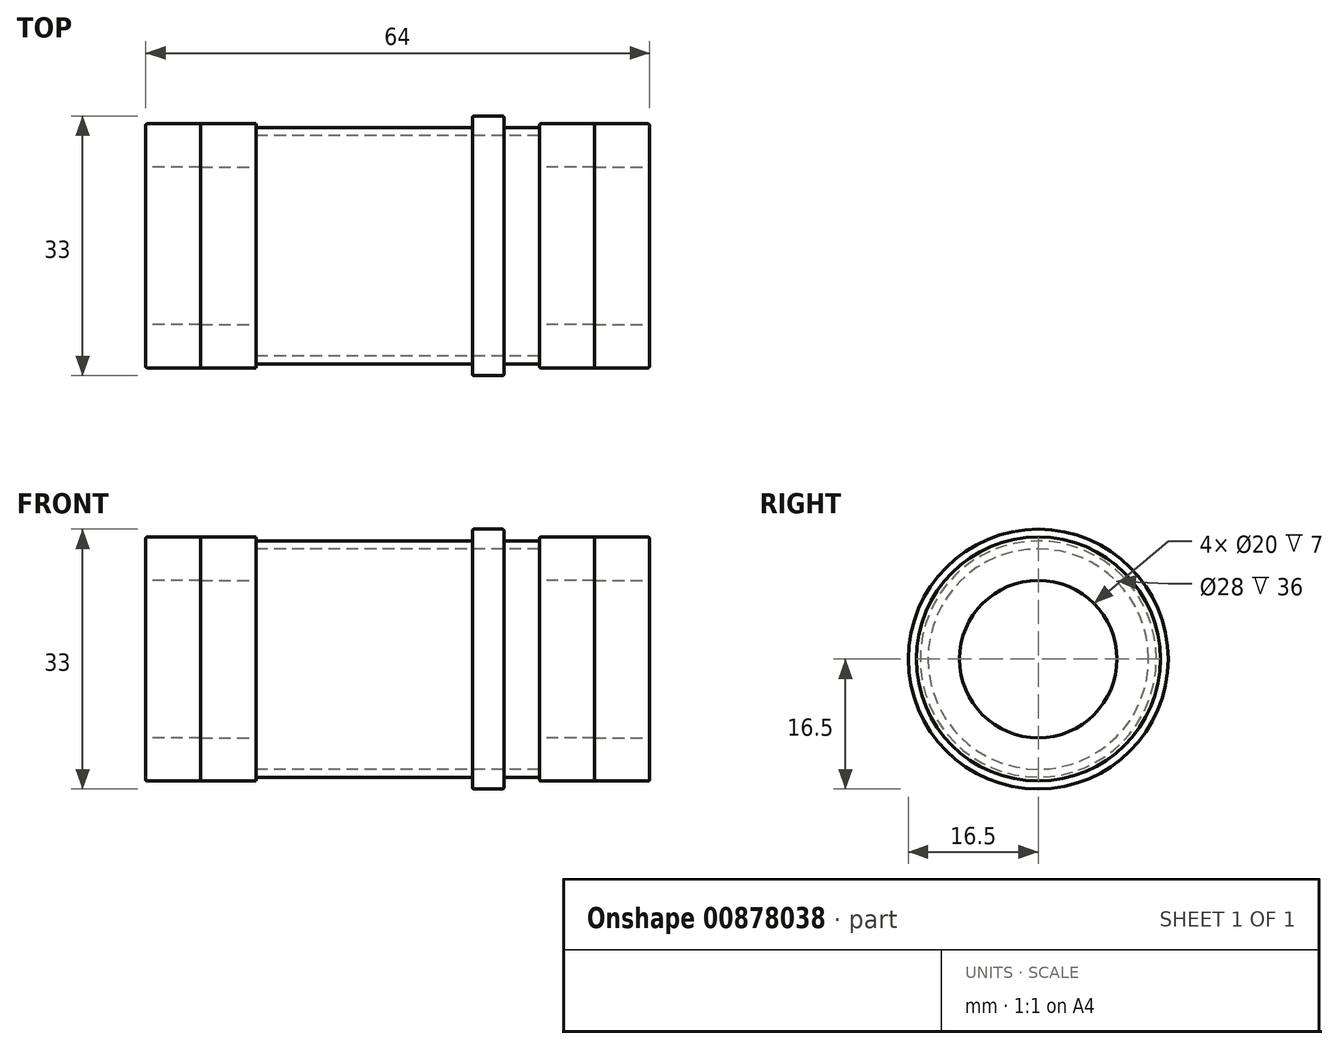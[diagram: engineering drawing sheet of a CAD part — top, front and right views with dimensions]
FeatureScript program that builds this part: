
annotation { "Feature Type Name" : "Feature", "Feature Type Description" : "" }
export const myFeature = defineFeature(function(context is Context, id is Id, definition is map)
    precondition{}
    {
        {
            var Q0;
            Q0=qCreatedBy(makeId("Right.planeOp"),FACE);
            var sketch = newSketch(context, id + "F0", { "sketchPlane" : qUnion([Q0])});
            skCircle(sketch, "E0", {"center": v(0, 0) * mm, "radius": 15 * mm});
            skCircle(sketch, "E1", {"center": v(0, 0) * mm, "radius": 14 * mm});
            skSolve(sketch);
        }
        {
            var Q0;
            Q0=makeQuery(id+"F0.imprint","IMPRINT",FACE,{"disambiguationData":[TD([[makeQuery(id+"F0.imprint","IMPRINT",EDGE,{"derivedFrom":sQuery(id+"F0.wireOp",EDGE,"E0")}),1.0]])]});
            extrude(context, id + "F1", {"entities" : qUnion([Q0]), "depth" : 36 * mm, "offsetDistance" : 25 * mm});
        }
        {
            var Q0;
            Q0=qCreatedBy(makeId("Right.planeOp"),FACE);
            var sketch = newSketch(context, id + "F2", { "sketchPlane" : qUnion([Q0])});
            skCircle(sketch, "E2", {"center": v(0, 0) * mm, "radius": 10 * mm});
            skCircle(sketch, "E3", {"center": v(0, 0) * mm, "radius": 15.5 * mm});
            skSolve(sketch);
        }
        {
            var Q0;
            Q0=makeQuery(id+"F2.imprint","IMPRINT",FACE,{"disambiguationData":[TD([[makeQuery(id+"F2.imprint","IMPRINT",EDGE,{"derivedFrom":sQuery(id+"F2.wireOp",EDGE,"E2")}),-1.0]])]});
            extrude(context, id + "F3", {"entities" : qUnion([Q0]), "oppositeDirection" : true, "depth" : 7 * mm, "offsetDistance" : 25 * mm});
        }
        {
            var Q0;
            Q0=makeQuery(id+"F3.opExtrude","SWEPT_BODY",BODY,{"disambiguationData":[OSD([sQuery(id+"F2.wireOp",EDGE,"E2"),sQuery(id+"F2.wireOp",EDGE,"E3")])]});
            var Q1;
            Q1=makeQuery(id+"F3.opExtrude","CAP_FACE",FACE,{"disambiguationData":[OSD([sQuery(id+"F2.wireOp",EDGE,"E2"),sQuery(id+"F2.wireOp",EDGE,"E3")])],"isStart":false});
            mirror(context, id + "F4", {"entities" : qUnion([Q0]), "mirrorPlane" : qUnion([Q1])});
        }
        {
            var Q0;
            Q0=makeQuery(id+"F3.opExtrude","SWEPT_BODY",BODY,{"disambiguationData":[OSD([sQuery(id+"F2.wireOp",EDGE,"E2"),sQuery(id+"F2.wireOp",EDGE,"E3")])]});
            var Q1;
            Q1=makeQuery(id+"F4.opPattern","COPY",BODY,{"derivedFrom":makeQuery(id+"F3.opExtrude","SWEPT_BODY",BODY,{"disambiguationData":[OSD([sQuery(id+"F2.wireOp",EDGE,"E2"),sQuery(id+"F2.wireOp",EDGE,"E3")])]}),"instanceName":"1"});
            var Q2;
            Q2=makeQuery(id+"F1.opExtrude","CAP_FACE",FACE,{"disambiguationData":[OSD([sQuery(id+"F0.wireOp",EDGE,"E0"),sQuery(id+"F0.wireOp",EDGE,"E1")])],"isStart":false});
            mirror(context, id + "F5", {"entities" : qUnion([Q0, Q1]), "mirrorPlane" : qUnion([Q2])});
        }
        {
            var Q0;
            Q0=makeQuery(id+"F5.opPattern","COPY",BODY,{"derivedFrom":makeQuery(id+"F3.opExtrude","SWEPT_BODY",BODY,{"disambiguationData":[OSD([sQuery(id+"F2.wireOp",EDGE,"E2"),sQuery(id+"F2.wireOp",EDGE,"E3")])]}),"instanceName":"1"});
            var Q1;
            Q1=makeQuery(id+"F5.opPattern","COPY",BODY,{"derivedFrom":makeQuery(id+"F4.opPattern","COPY",BODY,{"derivedFrom":makeQuery(id+"F3.opExtrude","SWEPT_BODY",BODY,{"disambiguationData":[OSD([sQuery(id+"F2.wireOp",EDGE,"E2"),sQuery(id+"F2.wireOp",EDGE,"E3")])]}),"instanceName":"1"}),"instanceName":"1"});
            var Q2;
            Q2=makeQuery(id+"F1.opExtrude","SWEPT_FACE",FACE,{"disambiguationData":[OSD([sQuery(id+"F0.wireOp",EDGE,"E0")])]});
            transform(context, id + "F6", {"entities" : qUnion([Q0, Q1]), "transformType" : TransformType.TRANSLATION_DISTANCE, "transformDirection" : qUnion([Q2]), "distance" : 36 * mm, "makeCopy" : false});
        }
        {
            var Q0;
            Q0=qCreatedBy(makeId("Front.planeOp"),FACE);
            var sketch = newSketch(context, id + "F7", { "sketchPlane" : qUnion([Q0])});
            skLineSegment(sketch, "E4.bottom", {"start": v(31.5, 15) * mm, "end": v(27.5, 15) * mm});
            skLineSegment(sketch, "E4.top", {"start": v(31.5, 16.5) * mm, "end": v(27.5, 16.5) * mm});
            skLineSegment(sketch, "E4.left", {"start": v(31.5, 15) * mm, "end": v(31.5, 16.5) * mm});
            skLineSegment(sketch, "E4.right", {"start": v(27.5, 15) * mm, "end": v(27.5, 16.5) * mm});
            skSolve(sketch);
        }
        {
            var Q0;
            Q0=makeQuery(id+"F7.imprint","IMPRINT",FACE,{"disambiguationData":[TD([[makeQuery(id+"F7.imprint","IMPRINT",EDGE,{"derivedFrom":sQuery(id+"F7.wireOp",EDGE,"E4.bottom")}),-1.0]])]});
            var Q1;
            Q1=makeQuery(id+"F1.opExtrude","SWEPT_FACE",FACE,{"disambiguationData":[OSD([sQuery(id+"F0.wireOp",EDGE,"E0")])]});
            revolve(context, id + "F8", {"operationType" : NewBodyOperationType.ADD, "surfaceOperationType" : NewSurfaceOperationType.NEW, "entities" : qUnion([Q0]), "axis" : qUnion([Q1]), "revolveType" : RevolveType.FULL});
        }
        {
            var Q0;
            Q0=makeQuery(id+"F5.opPattern","COPY",EDGE,{"derivedFrom":makeQuery(id+"F4.opPattern","COPY",EDGE,{"derivedFrom":makeQuery(id+"F3.opExtrude","CAP_EDGE",EDGE,{"disambiguationData":[OSD([sQuery(id+"F2.wireOp",EDGE,"E3")])],"isStart":true}),"instanceName":"1"}),"instanceName":"1"});
            var Q1;
            Q1=makeQuery(id+"F5.opPattern","COPY",EDGE,{"derivedFrom":makeQuery(id+"F3.opExtrude","CAP_EDGE",EDGE,{"disambiguationData":[OSD([sQuery(id+"F2.wireOp",EDGE,"E3")])],"isStart":true}),"instanceName":"1"});
            var Q2;
            Q2=makeQuery(id+"F4.opPattern","COPY",EDGE,{"derivedFrom":makeQuery(id+"F3.opExtrude","CAP_EDGE",EDGE,{"disambiguationData":[OSD([sQuery(id+"F2.wireOp",EDGE,"E3")])],"isStart":true}),"instanceName":"1"});
            var Q3;
            Q3=makeQuery(id+"F1.opExtrude","CAP_EDGE",EDGE,{"disambiguationData":[OSD([sQuery(id+"F0.wireOp",EDGE,"E0")])],"isStart":true});
            var Q4;
            Q4=makeQuery(id+"F8.opRevolve","SWEPT_EDGE",EDGE,{"disambiguationData":[OSD([sQuery(id+"F7.wireOp",EDGE,"E4.top"),sQuery(id+"F7.wireOp",EDGE,"E4.left")])]});
            var Q5;
            Q5=makeQuery(id+"F8.opRevolve","SWEPT_EDGE",EDGE,{"disambiguationData":[OSD([sQuery(id+"F7.wireOp",EDGE,"E4.top"),sQuery(id+"F7.wireOp",EDGE,"E4.right")])]});
            var Q6;
            Q6=makeQuery(id+"F8.opRevolve","SWEPT_EDGE",EDGE,{"disambiguationData":[OSD([sQuery(id+"F7.wireOp",EDGE,"E4.bottom"),sQuery(id+"F7.wireOp",EDGE,"E4.right")])]});
            var Q7;
            Q7=makeQuery(id+"F8.opRevolve","SWEPT_EDGE",EDGE,{"disambiguationData":[OSD([sQuery(id+"F7.wireOp",EDGE,"E4.bottom"),sQuery(id+"F7.wireOp",EDGE,"E4.left")])]});
            fillet(context, id + "F9", {"entities" : qUnion([Q0, Q1, Q2, Q3, Q4, Q5, Q6, Q7]), "tangentPropagation" : true, "radius" : .2 * mm, "defaultsChanged" : false, "vertexSettings" : [], "allowEdgeOverflow" : false});
        }
    });
